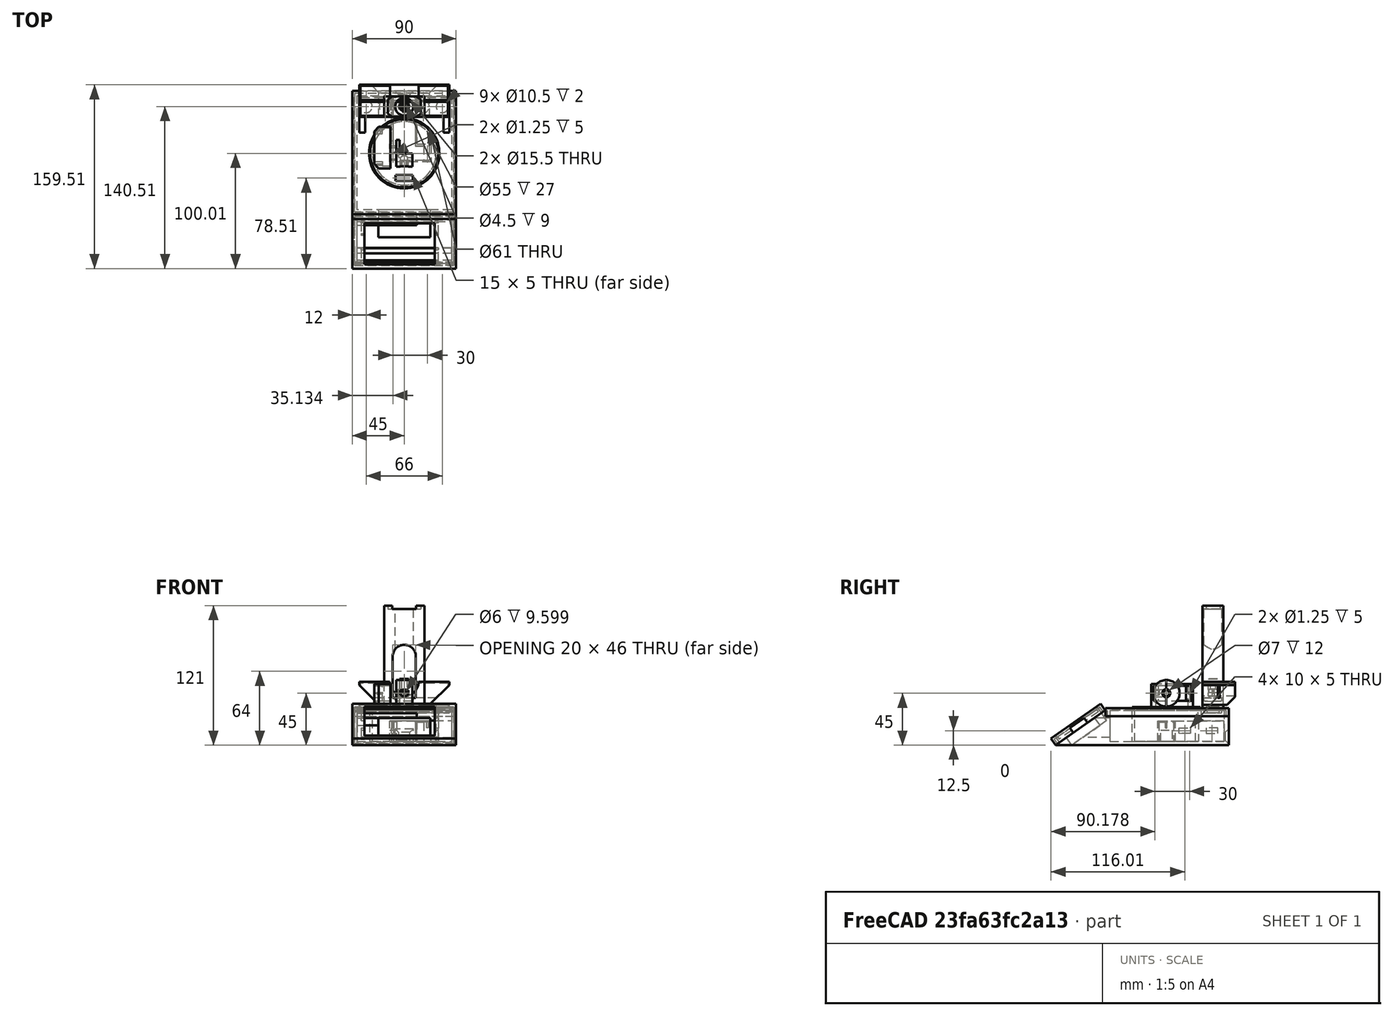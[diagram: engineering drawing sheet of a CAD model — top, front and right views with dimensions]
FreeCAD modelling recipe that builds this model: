
FCSTD DOCUMENT  (FreeCAD 0.18R16131 (Git))
Label: Laser_Projection_Microscope
License: All rights reserved
LicenseURL: http://en.wikipedia.org/wiki/All_rights_reserved
objects: Sketcher::SketchObject×63, PartDesign::Pocket×45, PartDesign::Pad×17, PartDesign::Body×8, Mesh::Feature×6, PartDesign::Chamfer×3, PartDesign::LinearPattern×3, PartDesign::Fillet×1
note: 202 computed .brp shape members not serialized (recipe doc carries the construction recipe); baked Part::Feature solids carry a one-line shape summary decoded from their .brp

FEATURE [Mesh::Feature] Nextion_2_4  label="Nextion 2.4"
  Placement = pos=(0,98.8389,144.254) rot=(0.287968,0.287968,-0.913318;1.66134rad)
FEATURE [Mesh::Feature] Arduino_Nano_wo_Mounts
  Placement = pos=(4.9631e-12,17,4) rot=(0,0,1;3.14159rad)
FEATURE [Sketcher::SketchObject] Sketch004  label="Sketch_Rect-Base-Cut"
  MapMode = 5
  Placement = pos=(45,0,0) rot=(0.57735,0.57735,0.57735;2.0944rad)
  sketch-geometry (3):
    g0: LineSegment StartX=-107 StartY=0 StartZ=0 EndX=-107 EndY=30 EndZ=0
    g1: LineSegment StartX=-107 StartY=30 StartZ=0 EndX=-64 EndY=30 EndZ=0
    g2: LineSegment StartX=-64 StartY=30 StartZ=0 EndX=-107 EndY=0 EndZ=0
  constraints (9):
    c: PointOnObject(g0,g-1)
    c: Vertical(g0)
    c: Coincident(g0,g1)
    c: Horizontal(g1)
    c: Coincident(g1,g2)
    c: Coincident(g2,g0)
    c: DistanceY(g0,g0) = 30
    c: DistanceX(g0,g-1) = 107
    c: DistanceX(g1,g1) = 43
FEATURE [Sketcher::SketchObject] Sketch019  label="Sketch_Cap-Screen-Base"
  MapMode = 5
  Support = -> [XY_Plane001]
  sketch-geometry (4):
    g0: LineSegment StartX=-45 StartY=52.43 StartZ=0 EndX=45 EndY=52.43 EndZ=0
    g1: LineSegment StartX=45 StartY=52.43 StartZ=0 EndX=45 EndY=0 EndZ=0
    g2: LineSegment StartX=45 StartY=0 StartZ=0 EndX=-45 EndY=0 EndZ=0
    g3: LineSegment StartX=-45 StartY=0 StartZ=0 EndX=-45 EndY=52.43 EndZ=0
  constraints (11):
    c: Coincident(g0,g1)
    c: Coincident(g1,g2)
    c: Coincident(g2,g3)
    c: Coincident(g3,g0)
    c: Horizontal(g0)
    c: Horizontal(g2)
    c: Vertical(g1)
    c: Vertical(g3)
    c: Symmetric(g2,g1,g-1)
    c: DistanceX(g2,g2) = 90
    c: DistanceY(g3,g3) = 52.43
FEATURE [PartDesign::Pad] Pad008  label="Pad_Cap-Screen-Base"
  Length = 7
  Length2 = 100
  Profile = -> Sketch019
  Type = 0
FEATURE [Sketcher::SketchObject] Sketch020  label="Sketch_Cap-Screen-Base-Hole"
  MapMode = 5
  Placement = pos=(0,0,0) rot=(1,0,0;3.14159rad)
  Support = -> [Pad008]
  sketch-geometry (4):
    g0: LineSegment StartX=-43 StartY=-2 StartZ=0 EndX=43 EndY=-2 EndZ=0
    g1: LineSegment StartX=43 StartY=-2 StartZ=0 EndX=43 EndY=-50.43 EndZ=0
    g2: LineSegment StartX=43 StartY=-50.43 StartZ=0 EndX=-43 EndY=-50.43 EndZ=0
    g3: LineSegment StartX=-43 StartY=-50.43 StartZ=0 EndX=-43 EndY=-2 EndZ=0
  constraints (11):
    c: Coincident(g0,g1)
    c: Coincident(g1,g2)
    c: Coincident(g2,g3)
    c: Coincident(g3,g0)
    c: Horizontal(g2)
    c: Vertical(g1)
    c: Vertical(g3)
    c: Symmetric(g0,g0,g-2)
    c: DistanceY(g0,g-1) = 2
    c: DistanceY(g3,g3) = 48.43
    c: DistanceX(g0,g0) = 86
FEATURE [PartDesign::Pocket] Pocket010  label="Pocket_Cap-Screen-Base"
  BaseFeature = -> Pad008
  Length = 5
  Length2 = 100
  Profile = -> Sketch020
  Type = 0
FEATURE [Sketcher::SketchObject] Sketch021  label="Sketch_Cap-Screen-Screen"
  MapMode = 5
  Placement = pos=(0,0,7) rot=(0,0,1;0rad)
  Support = -> [Pocket010]
  sketch-geometry (4):
    g0: LineSegment StartX=-34.5 StartY=48 StartZ=0 EndX=26.5 EndY=48 EndZ=0
    g1: LineSegment StartX=26.5 StartY=48 StartZ=0 EndX=26.5 EndY=4.5 EndZ=0
    g2: LineSegment StartX=26.5 StartY=4.5 StartZ=0 EndX=-34.5 EndY=4.5 EndZ=0
    g3: LineSegment StartX=-34.5 StartY=4.5 StartZ=0 EndX=-34.5 EndY=48 EndZ=0
  constraints (11):
    c: Coincident(g0,g1)
    c: Coincident(g1,g2)
    c: Coincident(g2,g3)
    c: Coincident(g3,g0)
    c: Horizontal(g2)
    c: Vertical(g1)
    c: Vertical(g3)
    c: DistanceY(g-1,g2) = 4.5
    c: DistanceY(g3,g3) = 43.5
    c: DistanceX(g2,g2) = 61
    c: DistanceX(g2,g-1) = 34.5
FEATURE [Sketcher::SketchObject] Sketch030  label="Sketch_Cap-Screen-Screen-Spacers"
  MapMode = 5
  Placement = pos=(0,0,5) rot=(1,0,0;3.14159rad)
  Support = -> [Pocket010]
  sketch-geometry (4):
    g0: LineSegment StartX=-37.5 StartY=-5.5 StartZ=0 EndX=29.5 EndY=-5.5 EndZ=0
    g1: LineSegment StartX=29.5 StartY=-5.5 StartZ=0 EndX=29.5 EndY=-47 EndZ=0
    g2: LineSegment StartX=29.5 StartY=-47 StartZ=0 EndX=-37.5 EndY=-47 EndZ=0
    g3: LineSegment StartX=-37.5 StartY=-47 StartZ=0 EndX=-37.5 EndY=-5.5 EndZ=0
  constraints (11):
    c: Coincident(g0,g1)
    c: Coincident(g1,g2)
    c: Coincident(g2,g3)
    c: Coincident(g3,g0)
    c: Horizontal(g2)
    c: Vertical(g1)
    c: Vertical(g3)
    c: DistanceY(g3,g3) = 41.5
    c: DistanceX(g2,g2) = 67
    c: DistanceY(g0,g-1) = 5.5
    c: DistanceX(g2,g-1) = 37.5
FEATURE [PartDesign::Pad] Pad011  label="Pad_Cap-Screen-Screen-Spacers"
  BaseFeature = -> Pocket010
  Length = 2.5
  Length2 = 100
  Profile = -> Sketch030
  Type = 0
FEATURE [PartDesign::Pocket] Pocket011  label="Pocket_Cap-Screen-Screen"
  BaseFeature = -> Pad011
  Length = 5
  Length2 = 100
  Profile = -> Sketch021
  Type = 1
FEATURE [Sketcher::SketchObject] Sketch029  label="Sketch_Cap-Screen_Hole-Cables"
  MapMode = 5
  Placement = pos=(0,0,0) rot=(1,0,0;3.14159rad)
  Support = -> [Pocket011]
  sketch-geometry (4):
    g0: LineSegment StartX=-45 StartY=-18.71 StartZ=0 EndX=45 EndY=-18.71 EndZ=0
    g1: LineSegment StartX=45 StartY=-18.71 StartZ=0 EndX=45 EndY=-33.71 EndZ=0
    g2: LineSegment StartX=45 StartY=-33.71 StartZ=0 EndX=-45 EndY=-33.71 EndZ=0
    g3: LineSegment StartX=-45 StartY=-33.71 StartZ=0 EndX=-45 EndY=-18.71 EndZ=0
  constraints (12):
    c: Coincident(g0,g1)
    c: Coincident(g1,g2)
    c: Coincident(g2,g3)
    c: Coincident(g3,g0)
    c: Horizontal(g0)
    c: Horizontal(g2)
    c: Vertical(g1)
    c: Vertical(g3)
    c: DistanceY(g3,g3) = 15
    c: DistanceY(g0,g-1) = 18.71
    c: DistanceX(g0,g-1) = 45
    c: DistanceX(g2,g2) = 90
FEATURE [PartDesign::Pocket] Pocket016  label="Pocket_Cap-Screen_Hole-Cables"
  BaseFeature = -> Pocket011
  Length = 5
  Length2 = 100
  Profile = -> Sketch029
  Type = 0
FEATURE [PartDesign::Body] Body001  label="Body_Cap-Screen"
  Group = -> [Sketch019,Pad008,Sketch020,Pocket010,Pad011,Sketch030,Sketch021,Pocket011,Sketch029,Pocket016]
  Origin = -> Origin001
  Placement = pos=(0,-107,0) rot=(1,0,0;0.60912rad)
  Tip = -> Pocket016
FEATURE [Sketcher::SketchObject] Sketch033
  MapMode = 5
  Placement = pos=(0,0,2) rot=(0,0,1;0rad)
  sketch-geometry (3):
    g0: LineSegment StartX=-41 StartY=38.816 StartZ=0 EndX=41 EndY=-60.184 EndZ=0
    g1: LineSegment StartX=41 StartY=38.816 StartZ=0 EndX=-41 EndY=-60.184 EndZ=0
    g2: Circle CenterX=0.0132459 CenterY=-10.7 CenterZ=0 NormalX=0 NormalY=0 NormalZ=1 AngleXU=0 Radius=30
  constraints (7):
    c: Symmetric(g0,g1,g-2)
    c: Symmetric(g1,g0,g-2)
    c: DistanceX(g0,g1) = 82
    c: DistanceY(g1,g0) = 99
    c: PointOnObject(g2,g0)
    c: Diameter(g2) = 60
    c: DistanceY(g2,g-1) = 10.7
FEATURE [Mesh::Feature] Servo  label="Servo_Turn-Table"
  Placement = pos=(5.2,-11,3) rot=(0,0,1;0rad)
FEATURE [Sketcher::SketchObject] Sketch043  label="Sketch_Cap-Base"
  MapMode = 5
  Support = -> [XY_Plane002]
  sketch-geometry (4):
    g0: LineSegment StartX=-45 StartY=43.1 StartZ=0 EndX=45 EndY=43.1 EndZ=0
    g1: LineSegment StartX=45 StartY=43.1 StartZ=0 EndX=45 EndY=-63.8 EndZ=0
    g2: LineSegment StartX=45 StartY=-63.8 StartZ=0 EndX=-45 EndY=-63.8 EndZ=0
    g3: LineSegment StartX=-45 StartY=-63.8 StartZ=0 EndX=-45 EndY=43.1 EndZ=0
  constraints (11):
    c: Coincident(g0,g1)
    c: Coincident(g1,g2)
    c: Coincident(g2,g3)
    c: Coincident(g3,g0)
    c: Horizontal(g2)
    c: Vertical(g1)
    c: Vertical(g3)
    c: DistanceX(g0,g0) = 90
    c: DistanceY(g3,g3) = 106.9
    c: DistanceY(g-1,g0) = 43.1
    c: Symmetric(g0,g0,g-2)
FEATURE [PartDesign::Pad] Pad015  label="Pad_Cap-Base"
  Length = 7
  Length2 = 100
  Profile = -> Sketch043
  Type = 0
FEATURE [Sketcher::SketchObject] Sketch044  label="Sketch_Cap-Hole"
  MapMode = 5
  Placement = pos=(0,0,0) rot=(1,0,0;3.14159rad)
  Support = -> [Pad015]
  sketch-geometry (4):
    g0: LineSegment StartX=-43 StartY=61.8 StartZ=0 EndX=43 EndY=61.8 EndZ=0
    g1: LineSegment StartX=43 StartY=61.8 StartZ=0 EndX=43 EndY=-41.1 EndZ=0
    g2: LineSegment StartX=43 StartY=-41.1 StartZ=0 EndX=-43 EndY=-41.1 EndZ=0
    g3: LineSegment StartX=-43 StartY=-41.1 StartZ=0 EndX=-43 EndY=61.8 EndZ=0
  constraints (11):
    c: Coincident(g0,g1)
    c: Coincident(g1,g2)
    c: Coincident(g2,g3)
    c: Coincident(g3,g0)
    c: Horizontal(g0)
    c: Vertical(g1)
    c: Vertical(g3)
    c: Symmetric(g2,g1,g-2)
    c: DistanceX(g2,g2) = 86
    c: DistanceY(g1,g1) = 102.9
    c: DistanceY(g2,g-1) = 41.1
FEATURE [PartDesign::Pocket] Pocket025  label="Pocket_Cap-Hole"
  BaseFeature = -> Pad015
  Length = 5
  Length2 = 100
  Profile = -> Sketch044
  Type = 0
FEATURE [Sketcher::SketchObject] Sketch045  label="Sketch_Cap-Circular-Hole"
  MapMode = 5
  Placement = pos=(0,0,7) rot=(0,0,1;0rad)
  Support = -> [Pocket025]
  sketch-geometry (1):
    g0: Circle CenterX=0 CenterY=-11 CenterZ=0 NormalX=0 NormalY=0 NormalZ=1 AngleXU=0 Radius=30.5
  constraints (3):
    c: PointOnObject(g0,g-2)
    c: Diameter(g0) = 61
    c: DistanceY(g0,g-1) = 11
FEATURE [PartDesign::Pocket] Pocket026  label="Pocket_Cap-Circular-Hole"
  BaseFeature = -> Pocket025
  Length = 5
  Length2 = 100
  Profile = -> Sketch045
  Type = 2
FEATURE [Sketcher::SketchObject] Sketch046  label="Sketch_Turn-Table-Base"
  MapMode = 5
  Support = -> [XY_Plane003]
  sketch-geometry (1):
    g0: Circle CenterX=0 CenterY=-11 CenterZ=0 NormalX=0 NormalY=0 NormalZ=1 AngleXU=0 Radius=29.5
  constraints (3):
    c: PointOnObject(g0,g-2)
    c: DistanceY(g0,g-1) = 11
    c: Diameter(g0) = 59
FEATURE [PartDesign::Pad] Pad016  label="Pad_Turn-Table-Base"
  Length = 3
  Length2 = 100
  Profile = -> Sketch046
  Type = 0
FEATURE [Sketcher::SketchObject] Sketch003  label="Sketch_Rect-Base"
  MapMode = 5
  Placement = pos=(0,0,0) rot=(1,0,0;3.14159rad)
  Support = -> [Pad016]
  sketch-geometry (4):
    g0: LineSegment StartX=-45 StartY=106.9 StartZ=0 EndX=45 EndY=106.9 EndZ=0
    g1: LineSegment StartX=45 StartY=106.9 StartZ=0 EndX=45 EndY=-43.1 EndZ=0
    g2: LineSegment StartX=45 StartY=-43.1 StartZ=0 EndX=-45 EndY=-43.1 EndZ=0
    g3: LineSegment StartX=-45 StartY=-43.1 StartZ=0 EndX=-45 EndY=106.9 EndZ=0
  constraints (11):
    c: Coincident(g0,g1)
    c: Coincident(g1,g2)
    c: Coincident(g2,g3)
    c: Coincident(g3,g0)
    c: Horizontal(g2)
    c: Vertical(g1)
    c: Vertical(g3)
    c: DistanceY(g1,g1) = 150
    c: DistanceX(g0,g0) = 90
    c: Symmetric(g0,g0,g-2)
    c: DistanceY(g-1,g0) = 106.9
FEATURE [PartDesign::Pad] Pad002  label="Pad_Rect-Base"
  Length = 30
  Length2 = 100
  Profile = -> Sketch003
  Reversed = true
  Type = 0
FEATURE [PartDesign::Pocket] Pocket001  label="Pocket_Rect-Base-Cut"
  BaseFeature = -> Pad002
  Length = 5
  Length2 = 100
  Profile = -> Sketch004
  Type = 1
FEATURE [Sketcher::SketchObject] Sketch005  label="Sketch_Rect-Base-Top"
  MapMode = 5
  Placement = pos=(0,-35.0309,50.211) rot=(1,0,0;0.609163rad)
  Support = -> [Pocket001]
  sketch-geometry (4):
    g0: LineSegment StartX=-43 StartY=-37.38 StartZ=0 EndX=43 EndY=-37.38 EndZ=0
    g1: LineSegment StartX=43 StartY=-37.38 StartZ=0 EndX=43 EndY=-85.81 EndZ=0
    g2: LineSegment StartX=43 StartY=-85.81 StartZ=0 EndX=-43 EndY=-85.81 EndZ=0
    g3: LineSegment StartX=-43 StartY=-85.81 StartZ=0 EndX=-43 EndY=-37.38 EndZ=0
  constraints (11):
    c: Coincident(g0,g1)
    c: Coincident(g1,g2)
    c: Coincident(g2,g3)
    c: Coincident(g3,g0)
    c: Horizontal(g0)
    c: Vertical(g1)
    c: Vertical(g3)
    c: Symmetric(g2,g1,g-2)
    c: DistanceY(g3,g3) = 48.43
    c: DistanceX(g0,g0) = 86
    c: DistanceY(g0,g-1) = 37.38
FEATURE [PartDesign::Pad] Pad003  label="Pad_Rect-Base-Cut"
  BaseFeature = -> Pocket001
  Length = 5
  Length2 = 100
  Profile = -> Sketch005
  Type = 0
FEATURE [Sketcher::SketchObject] Sketch006  label="Sketch_Rect-Base-Hole"
  MapMode = 5
  Placement = pos=(0,-37.8918,54.3116) rot=(1,0,0;0.609163rad)
  Support = -> [Pad003]
  sketch-geometry (4):
    g0: LineSegment StartX=-41 StartY=-39.38 StartZ=0 EndX=41 EndY=-39.38 EndZ=0
    g1: LineSegment StartX=41 StartY=-39.38 StartZ=0 EndX=41 EndY=-83.81 EndZ=0
    g2: LineSegment StartX=41 StartY=-83.81 StartZ=0 EndX=-41 EndY=-83.81 EndZ=0
    g3: LineSegment StartX=-41 StartY=-83.81 StartZ=0 EndX=-41 EndY=-39.38 EndZ=0
  constraints (11):
    c: Coincident(g0,g1)
    c: Coincident(g1,g2)
    c: Coincident(g2,g3)
    c: Coincident(g3,g0)
    c: Horizontal(g0)
    c: Vertical(g1)
    c: Vertical(g3)
    c: Symmetric(g2,g1,g-2)
    c: DistanceY(g3,g3) = 44.43
    c: DistanceX(g0,g0) = 82
    c: DistanceY(g0,g-1) = 39.38
FEATURE [PartDesign::Pocket] Pocket002  label="Pocket_Rect-Base-Hole"
  BaseFeature = -> Pad003
  Length = 5
  Length2 = 100
  Profile = -> Sketch006
  Type = 0
FEATURE [Sketcher::SketchObject] Sketch007  label="Sketch_Rect-Base-Cables"
  MapMode = 5
  Placement = pos=(0,-35.0309,50.211) rot=(1,0,0;0.609163rad)
  Support = -> [Pocket002]
  sketch-geometry (4):
    g0: LineSegment StartX=-41 StartY=-46.595 StartZ=0 EndX=41 EndY=-46.595 EndZ=0
    g1: LineSegment StartX=41 StartY=-46.595 StartZ=0 EndX=41 EndY=-76.595 EndZ=0
    g2: LineSegment StartX=41 StartY=-76.595 StartZ=0 EndX=-41 EndY=-76.595 EndZ=0
    g3: LineSegment StartX=-41 StartY=-76.595 StartZ=0 EndX=-41 EndY=-46.595 EndZ=0
  constraints (11):
    c: Coincident(g0,g1)
    c: Coincident(g1,g2)
    c: Coincident(g2,g3)
    c: Coincident(g3,g0)
    c: Horizontal(g2)
    c: Vertical(g1)
    c: Vertical(g3)
    c: DistanceX(g0,g0) = 82
    c: DistanceY(g3,g3) = 30
    c: Symmetric(g0,g0,g-2)
    c: DistanceY(g0,g-1) = 46.595
FEATURE [PartDesign::Pocket] Pocket003  label="Pocket_Rect-Base-Cables"
  BaseFeature = -> Pocket002
  Length = 8
  Length2 = 100
  Profile = -> Sketch007
  Type = 0
FEATURE [Sketcher::SketchObject] Sketch009  label="Sketch_Rect-Base-SD"
  MapMode = 5
  Placement = pos=(0,-35.0309,50.211) rot=(1,0,0;0.609163rad)
  Support = -> [Pocket003]
  sketch-geometry (4):
    g0: LineSegment StartX=11 StartY=-39.38 StartZ=0 EndX=41 EndY=-39.38 EndZ=0
    g1: LineSegment StartX=41 StartY=-39.38 StartZ=0 EndX=41 EndY=-54.38 EndZ=0
    g2: LineSegment StartX=41 StartY=-54.38 StartZ=0 EndX=11 EndY=-54.38 EndZ=0
    g3: LineSegment StartX=11 StartY=-54.38 StartZ=0 EndX=11 EndY=-39.38 EndZ=0
  constraints (12):
    c: Coincident(g0,g1)
    c: Coincident(g1,g2)
    c: Coincident(g2,g3)
    c: Coincident(g3,g0)
    c: Horizontal(g0)
    c: Vertical(g1)
    c: Vertical(g3)
    c: DistanceY(g3,g3) = 15
    c: DistanceX(g0,g0) = 30
    c: DistanceY(g0,g-1) = 39.38
    c: DistanceX(g-1,g0) = 41
    c: Horizontal(g2)
FEATURE [PartDesign::Pocket] Pocket004  label="Pocket_Rect-Base-SD"
  BaseFeature = -> Pocket003
  Length = 8
  Length2 = 100
  Profile = -> Sketch009
  Type = 0
FEATURE [Sketcher::SketchObject] Sketch  label="Sketch_Rect-Base-Connection"
  AttachmentOffset = pos=(0,0,-47) rot=(0,0,1;0rad)
  MapMode = 5
  Placement = pos=(0,-59.9,-1.04e-14) rot=(1,0,0;1.5708rad)
  Support = -> [Pocket004]
  sketch-geometry (4):
    g0: LineSegment StartX=-22.5 StartY=23.5 StartZ=0 EndX=22.5 EndY=23.5 EndZ=0
    g1: LineSegment StartX=22.5 StartY=23.5 StartZ=0 EndX=22.5 EndY=6.5 EndZ=0
    g2: LineSegment StartX=22.5 StartY=6.5 StartZ=0 EndX=-22.5 EndY=6.5 EndZ=0
    g3: LineSegment StartX=-22.5 StartY=6.5 StartZ=0 EndX=-22.5 EndY=23.5 EndZ=0
  constraints (11):
    c: Coincident(g0,g1)
    c: Coincident(g1,g2)
    c: Coincident(g2,g3)
    c: Coincident(g3,g0)
    c: Horizontal(g2)
    c: Vertical(g1)
    c: Vertical(g3)
    c: DistanceY(g-1,g2) = 6.5
    c: DistanceY(g1,g1) = 17
    c: DistanceX(g0,g0) = 45
    c: Symmetric(g0,g0,g-2)
FEATURE [PartDesign::Pocket] Pocket  label="Pocket_Rect-Base-Connection"
  BaseFeature = -> Pocket004
  Length = 5
  Length2 = 100
  Profile = -> Sketch
  Reversed = true
  Type = 1
FEATURE [Sketcher::SketchObject] Sketch034  label="Sketch_Rect-Base-Central-Lowering-Hole"
  MapMode = 5
  Placement = pos=(0,0,30) rot=(0,0,1;0rad)
  Support = -> [Pocket]
  sketch-geometry (4):
    g0: LineSegment StartX=-45 StartY=43.1 StartZ=0 EndX=45 EndY=43.1 EndZ=0
    g1: LineSegment StartX=45 StartY=43.1 StartZ=0 EndX=45 EndY=-63.9 EndZ=0
    g2: LineSegment StartX=45 StartY=-63.9 StartZ=0 EndX=-45 EndY=-63.9 EndZ=0
    g3: LineSegment StartX=-45 StartY=-63.9 StartZ=0 EndX=-45 EndY=43.1 EndZ=0
  constraints (11):
    c: Coincident(g0,g1)
    c: Coincident(g1,g2)
    c: Coincident(g2,g3)
    c: Coincident(g3,g0)
    c: Horizontal(g2)
    c: Vertical(g1)
    c: Vertical(g3)
    c: Symmetric(g0,g0,g-2)
    c: DistanceX(g0,g0) = 90
    c: DistanceY(g-1,g0) = 43.1
    c: DistanceY(g1,g1) = 107
FEATURE [PartDesign::Pocket] Pocket017  label="Pocket_Rect-Base-Central-Lowering-Hole"
  BaseFeature = -> Pocket
  Length = 5
  Length2 = 100
  Profile = -> Sketch034
  Type = 0
FEATURE [Sketcher::SketchObject] Sketch031  label="Sketch_Rect-Base-Central-Top"
  MapMode = 5
  Placement = pos=(0,0,25) rot=(0,0,1;0rad)
  Support = -> [Pocket017]
  sketch-geometry (4):
    g0: LineSegment StartX=-43 StartY=41.1 StartZ=0 EndX=43 EndY=41.1 EndZ=0
    g1: LineSegment StartX=43 StartY=41.1 StartZ=0 EndX=43 EndY=-61.9 EndZ=0
    g2: LineSegment StartX=43 StartY=-61.9 StartZ=0 EndX=-43 EndY=-61.9 EndZ=0
    g3: LineSegment StartX=-43 StartY=-61.9 StartZ=0 EndX=-43 EndY=41.1 EndZ=0
  constraints (11):
    c: Coincident(g0,g1)
    c: Coincident(g1,g2)
    c: Coincident(g2,g3)
    c: Coincident(g3,g0)
    c: Horizontal(g2)
    c: Vertical(g1)
    c: Vertical(g3)
    c: Symmetric(g0,g0,g-2)
    c: DistanceX(g0,g0) = 86
    c: DistanceY(g-1,g0) = 41.1
    c: DistanceY(g1,g1) = 103
FEATURE [PartDesign::Pad] Pad  label="Pad_Rect-Base-Central-Top"
  BaseFeature = -> Pocket017
  Length = 5
  Length2 = 100
  Profile = -> Sketch031
  Type = 0
FEATURE [Sketcher::SketchObject] Sketch032  label="Sketch_Rect-Base-Central-Hole"
  MapMode = 5
  Placement = pos=(0,0,30) rot=(0,0,1;0rad)
  Support = -> [Pad]
  sketch-geometry (4):
    g0: LineSegment StartX=-41 StartY=39.1 StartZ=0 EndX=41 EndY=39.1 EndZ=0
    g1: LineSegment StartX=41 StartY=39.1 StartZ=0 EndX=41 EndY=-59.9 EndZ=0
    g2: LineSegment StartX=41 StartY=-59.9 StartZ=0 EndX=-41 EndY=-59.9 EndZ=0
    g3: LineSegment StartX=-41 StartY=-59.9 StartZ=0 EndX=-41 EndY=39.1 EndZ=0
  constraints (11):
    c: Coincident(g0,g1)
    c: Coincident(g1,g2)
    c: Coincident(g2,g3)
    c: Coincident(g3,g0)
    c: Horizontal(g2)
    c: Vertical(g1)
    c: Vertical(g3)
    c: Symmetric(g0,g0,g-2)
    c: DistanceX(g0,g0) = 82
    c: DistanceY(g-1,g0) = 39.1
    c: DistanceY(g1,g1) = 99
FEATURE [PartDesign::Pocket] Pocket018  label="Pocket_Rect-Base-Central-Hole"
  BaseFeature = -> Pad
  Length = 27
  Length2 = 100
  Profile = -> Sketch032
  Type = 0
FEATURE [Sketcher::SketchObject] Sketch036  label="Sketch_Rect-Base-Pad-Round"
  MapMode = 5
  Placement = pos=(0,0,3) rot=(0,0,1;0rad)
  Support = -> [Pocket018]
  sketch-geometry (1):
    g0: Circle CenterX=0 CenterY=-11 CenterZ=0 NormalX=0 NormalY=0 NormalZ=1 AngleXU=0 Radius=30
  constraints (3):
    c: PointOnObject(g0,g-2)
    c: Diameter(g0) = 60
    c: DistanceY(g0,g-1) = 11
FEATURE [PartDesign::Pad] Pad013  label="Pad_Rect-Base-Pad-Round"
  BaseFeature = -> Pocket018
  Length = 27
  Length2 = 100
  Profile = -> Sketch036
  Type = 0
FEATURE [Sketcher::SketchObject] Sketch037  label="Sketch_Rect-Base-Pad-Round-Hole"
  MapMode = 5
  Placement = pos=(0,0,30) rot=(0,0,1;0rad)
  Support = -> [Pad013]
  sketch-geometry (1):
    g0: Circle CenterX=0 CenterY=-11 CenterZ=0 NormalX=0 NormalY=0 NormalZ=1 AngleXU=0 Radius=27.5
  constraints (3):
    c: PointOnObject(g0,g-2)
    c: DistanceY(g0,g-1) = 11
    c: Diameter(g0) = 55
FEATURE [PartDesign::Pocket] Pocket019  label="Pocket_Rect-Base-Pad-Round-Hole"
  BaseFeature = -> Pad013
  Length = 27
  Length2 = 100
  Profile = -> Sketch037
  Type = 0
FEATURE [Sketcher::SketchObject] Sketch035  label="Sketch_Rect-Base-Pad-Elements"
  MapMode = 5
  Placement = pos=(0,0,3) rot=(0,0,1;0rad)
  Support = -> [Pocket019]
  sketch-geometry (8):
    g0: LineSegment StartX=-11 StartY=39 StartZ=0 EndX=11 EndY=39 EndZ=0
    g1: LineSegment StartX=11 StartY=39 StartZ=0 EndX=11 EndY=-3.04259 EndZ=0
    g2: LineSegment StartX=11 StartY=-3.04259 StartZ=0 EndX=23.2659 EndY=-3.04259 EndZ=0
    g3: LineSegment StartX=23.2659 StartY=-3.04259 StartZ=0 EndX=23.2659 EndY=-18.4793 EndZ=0
    g4: LineSegment StartX=23.2659 StartY=-18.4793 StartZ=0 EndX=-12.7089 EndY=-18.4793 EndZ=0
    g5: LineSegment StartX=-12.7089 StartY=-18.4793 StartZ=0 EndX=-12.7089 EndY=-3.04259 EndZ=0
    g6: LineSegment StartX=-12.7089 StartY=-3.04259 StartZ=0 EndX=-11 EndY=-3.04259 EndZ=0
    g7: LineSegment StartX=-11 StartY=-3.04259 StartZ=0 EndX=-11 EndY=39 EndZ=0
  constraints (18):
    c: Coincident(g0,g1)
    c: Vertical(g1)
    c: Coincident(g1,g2)
    c: Horizontal(g2)
    c: Coincident(g2,g3)
    c: Vertical(g3)
    c: Coincident(g3,g4)
    c: Horizontal(g4)
    c: Coincident(g4,g5)
    c: Vertical(g5)
    c: Coincident(g5,g6)
    c: Coincident(g6,g7)
    c: Coincident(g7,g0)
    c: DistanceY(g-1,g0) = 39
    c: Symmetric(g0,g0,g-2)
    c: DistanceX(g0,g0) = 22
    c: Symmetric(g6,g1,g-2)
    c: Equal(g5,g3)
FEATURE [PartDesign::Pad] Pad014  label="Pad_Rect-Base-Pad-Elements"
  BaseFeature = -> Pocket019
  Length = 18
  Length2 = 100
  Profile = -> Sketch035
  Type = 0
FEATURE [Sketcher::SketchObject] Sketch038  label="Sketch_Rect-Base-Pad-Elements-Hole1"
  MapMode = 5
  Placement = pos=(0,0,21) rot=(0,0,1;0rad)
  Support = -> [Pad014]
  sketch-geometry (8):
    g0: LineSegment StartX=-9.5 StartY=39 StartZ=0 EndX=9.5 EndY=39 EndZ=0
    g1: LineSegment StartX=9.5 StartY=39 StartZ=0 EndX=9.5 EndY=-4.75035 EndZ=0
    g2: LineSegment StartX=9.5 StartY=-4.75035 StartZ=0 EndX=16.9308 EndY=-4.75035 EndZ=0
    g3: LineSegment StartX=16.9308 StartY=-4.75035 StartZ=0 EndX=16.9308 EndY=-17.3252 EndZ=0
    g4: LineSegment StartX=16.9308 StartY=-17.3252 StartZ=0 EndX=-6.62122 EndY=-17.3252 EndZ=0
    g5: LineSegment StartX=-6.62122 StartY=-17.3252 StartZ=0 EndX=-6.62122 EndY=-4.75035 EndZ=0
    g6: LineSegment StartX=-6.62122 StartY=-4.75035 StartZ=0 EndX=-9.5 EndY=-4.75035 EndZ=0
    g7: LineSegment StartX=-9.5 StartY=-4.75035 StartZ=0 EndX=-9.5 EndY=39 EndZ=0
  constraints (18):
    c: Coincident(g0,g1)
    c: Vertical(g1)
    c: Coincident(g1,g2)
    c: Horizontal(g2)
    c: Coincident(g2,g3)
    c: Vertical(g3)
    c: Coincident(g3,g4)
    c: Horizontal(g4)
    c: Coincident(g4,g5)
    c: Vertical(g5)
    c: Coincident(g5,g6)
    c: Coincident(g6,g7)
    c: Coincident(g7,g0)
    c: DistanceY(g-1,g0) = 39
    c: Symmetric(g0,g0,g-2)
    c: DistanceX(g0,g0) = 19
    c: Symmetric(g6,g1,g-2)
    c: Equal(g5,g3)
FEATURE [PartDesign::Pocket] Pocket020  label="Pocket_Rect-Base-Pad-Elements-Hole1"
  BaseFeature = -> Pad014
  Length = 18
  Length2 = 100
  Profile = -> Sketch038
  Type = 0
FEATURE [Sketcher::SketchObject] Sketch039  label="Sketch_Rect-Base-Pad-Elements-Hole2"
  MapMode = 5
  Placement = pos=(0,0,21) rot=(0,0,1;0rad)
  Support = -> [Pocket020]
  sketch-geometry (4):
    g0: LineSegment StartX=-11.2081 StartY=-4.57742 StartZ=0 EndX=21.6941 EndY=-4.57742 EndZ=0
    g1: LineSegment StartX=21.6941 StartY=-4.57742 StartZ=0 EndX=21.6941 EndY=-17.3252 EndZ=0
    g2: LineSegment StartX=21.6941 StartY=-17.3252 StartZ=0 EndX=-11.2081 EndY=-17.3252 EndZ=0
    g3: LineSegment StartX=-11.2081 StartY=-17.3252 StartZ=0 EndX=-11.2081 EndY=-4.57742 EndZ=0
  constraints (8):
    c: Coincident(g0,g1)
    c: Coincident(g1,g2)
    c: Coincident(g2,g3)
    c: Coincident(g3,g0)
    c: Horizontal(g0)
    c: Horizontal(g2)
    c: Vertical(g1)
    c: Vertical(g3)
FEATURE [PartDesign::Pocket] Pocket021  label="Pocket_Rect-Base-Pad-Elements-Hole2"
  BaseFeature = -> Pocket020
  Length = 1
  Length2 = 100
  Profile = -> Sketch039
  Type = 0
FEATURE [Sketcher::SketchObject] Sketch040  label="Sketch_Rect-Base-Cable-Hole-Servo"
  MapMode = 5
  Placement = pos=(-12.7089,0,0) rot=(0.57735,-0.57735,-0.57735;2.0944rad)
  Support = -> [Pocket021]
  sketch-geometry (4):
    g0: LineSegment StartX=6 StartY=13 StartZ=0 EndX=16 EndY=13 EndZ=0
    g1: LineSegment StartX=16 StartY=13 StartZ=0 EndX=16 EndY=3 EndZ=0
    g2: LineSegment StartX=16 StartY=3 StartZ=0 EndX=6 EndY=3 EndZ=0
    g3: LineSegment StartX=6 StartY=3 StartZ=0 EndX=6 EndY=13 EndZ=0
  constraints (12):
    c: Coincident(g0,g1)
    c: Coincident(g1,g2)
    c: Coincident(g2,g3)
    c: Coincident(g3,g0)
    c: Horizontal(g0)
    c: Horizontal(g2)
    c: Vertical(g1)
    c: Vertical(g3)
    c: DistanceY(g-1,g1) = 3
    c: DistanceX(g-1,g2) = 6
    c: DistanceX(g2,g2) = 10
    c: DistanceY(g1,g1) = 10
FEATURE [PartDesign::Pocket] Pocket022  label="Pocket_Rect-Base-Cable-Hole-Servo"
  BaseFeature = -> Pocket021
  Length = 5
  Length2 = 100
  Profile = -> Sketch040
  Type = 2
FEATURE [Sketcher::SketchObject] Sketch041  label="Sketch_Rect-Base-Cable-Hole-String"
  MapMode = 5
  Placement = pos=(-11,0,0) rot=(0.57735,-0.57735,-0.57735;2.0944rad)
  Support = -> [Pocket022]
  sketch-geometry (8):
    g0: LineSegment StartX=-10 StartY=15 StartZ=0 EndX=0 EndY=15 EndZ=0
    g1: LineSegment StartX=0 StartY=15 StartZ=0 EndX=0 EndY=10 EndZ=0
    g2: LineSegment StartX=0 StartY=10 StartZ=0 EndX=-10 EndY=10 EndZ=0
    g3: LineSegment StartX=-10 StartY=10 StartZ=0 EndX=-10 EndY=15 EndZ=0
    g4: LineSegment StartX=-33.5394 StartY=15 StartZ=0 EndX=-23.5394 EndY=15 EndZ=0
    g5: LineSegment StartX=-23.5394 StartY=15 StartZ=0 EndX=-23.5394 EndY=10 EndZ=0
    g6: LineSegment StartX=-23.5394 StartY=10 StartZ=0 EndX=-33.5394 EndY=10 EndZ=0
    g7: LineSegment StartX=-33.5394 StartY=10 StartZ=0 EndX=-33.5394 EndY=15 EndZ=0
  constraints (23):
    c: Coincident(g0,g1)
    c: Coincident(g1,g2)
    c: Coincident(g2,g3)
    c: Coincident(g3,g0)
    c: Horizontal(g0)
    c: Horizontal(g2)
    c: Vertical(g1)
    c: Vertical(g3)
    c: PointOnObject(g1,g-2)
    c: Coincident(g4,g5)
    c: Coincident(g5,g6)
    c: Coincident(g6,g7)
    c: Coincident(g7,g4)
    c: Horizontal(g4)
    c: Horizontal(g6)
    c: Vertical(g5)
    c: Vertical(g7)
    c: Equal(g5,g1)
    c: Equal(g0,g4)
    c: DistanceY(g-1,g1) = 10
    c: DistanceY(g-1,g5) = 10
    c: DistanceX(g4,g4) = 10
    c: DistanceY(g7,g7) = 5
FEATURE [PartDesign::Pocket] Pocket023  label="Pocket_Rect-Base-Cable-Hole-String"
  BaseFeature = -> Pocket022
  Length = 22
  Length2 = 100
  Profile = -> Sketch041
  Type = 0
FEATURE [Sketcher::SketchObject] Sketch042  label="Sketch_Rect-Base-Arduino-Hole"
  MapMode = 5
  Placement = pos=(0,43.1,0) rot=(0,0.707107,0.707107;3.14159rad)
  Support = -> [Pocket023]
  sketch-geometry (4):
    g0: LineSegment StartX=-5 StartY=11 StartZ=0 EndX=5 EndY=11 EndZ=0
    g1: LineSegment StartX=5 StartY=11 StartZ=0 EndX=5 EndY=4 EndZ=0
    g2: LineSegment StartX=5 StartY=4 StartZ=0 EndX=-5 EndY=4 EndZ=0
    g3: LineSegment StartX=-5 StartY=4 StartZ=0 EndX=-5 EndY=11 EndZ=0
  constraints (11):
    c: Coincident(g0,g1)
    c: Coincident(g1,g2)
    c: Coincident(g2,g3)
    c: Coincident(g3,g0)
    c: Horizontal(g2)
    c: Vertical(g1)
    c: Vertical(g3)
    c: Symmetric(g0,g0,g-2)
    c: DistanceX(g0,g0) = 10
    c: DistanceY(g1,g1) = 7
    c: DistanceY(g-1,g1) = 4
FEATURE [PartDesign::Pocket] Pocket024  label="Pocket_Rect-Base-Arduino-Hole"
  BaseFeature = -> Pocket023
  Length = 5
  Length2 = 100
  Profile = -> Sketch042
  Type = 2
FEATURE [PartDesign::Chamfer] Chamfer
  Base = -> Pocket024 [Edge31,Edge30,Edge32,Edge29]
  BaseFeature = -> Pocket024
  Size = 3
FEATURE [Sketcher::SketchObject] Sketch047  label="Sketch_Turn-Table-Hole-Servo"
  MapMode = 5
  Placement = pos=(0,0,0) rot=(1,0,0;3.14159rad)
  Support = -> [Pad016]
  sketch-geometry (1):
    g0: Circle CenterX=0 CenterY=11 CenterZ=0 NormalX=0 NormalY=0 NormalZ=1 AngleXU=0 Radius=2.25
  constraints (3):
    c: PointOnObject(g0,g-2)
    c: DistanceY(g0,g-1) = -11
    c: Diameter(g0) = 4.5
FEATURE [PartDesign::Pocket] Pocket027  label="Pocket_Turn-Table-Hole-Servo"
  BaseFeature = -> Pad016
  Length = 3
  Length2 = 100
  Profile = -> Sketch047
  Type = 0
FEATURE [Sketcher::SketchObject] Sketch048  label="Sketch_Turn-Table-Hole-Cables"
  MapMode = 5
  Placement = pos=(0,0,3) rot=(0,0,1;0rad)
  Support = -> [Pocket027]
  sketch-geometry (4):
    g0: LineSegment StartX=-7.5 StartY=-30 StartZ=0 EndX=7.5 EndY=-30 EndZ=0
    g1: LineSegment StartX=7.5 StartY=-30 StartZ=0 EndX=7.5 EndY=-35 EndZ=0
    g2: LineSegment StartX=7.5 StartY=-35 StartZ=0 EndX=-7.5 EndY=-35 EndZ=0
    g3: LineSegment StartX=-7.5 StartY=-35 StartZ=0 EndX=-7.5 EndY=-30 EndZ=0
  constraints (11):
    c: Coincident(g0,g1)
    c: Coincident(g1,g2)
    c: Coincident(g2,g3)
    c: Coincident(g3,g0)
    c: Horizontal(g2)
    c: Vertical(g1)
    c: Vertical(g3)
    c: Symmetric(g0,g0,g-2)
    c: DistanceX(g2,g2) = 15
    c: DistanceY(g1,g1) = 5
    c: DistanceY(g0,g-1) = 30
FEATURE [PartDesign::Pocket] Pocket028  label="Pocket_Turn-Table-Hole-Cables"
  BaseFeature = -> Pocket027
  Length = 5
  Length2 = 100
  Profile = -> Sketch048
  Type = 0
FEATURE [Sketcher::SketchObject] Sketch049  label="Sketch_Rect-Base-Screws"
  MapMode = 5
  Placement = pos=(0,0,20) rot=(0,0,1;0rad)
  Support = -> [Chamfer]
  sketch-geometry (2):
    g0: Circle CenterX=-9.86578 CenterY=-11 CenterZ=0 NormalX=0 NormalY=0 NormalZ=1 AngleXU=0 Radius=0.625
    g1: Circle CenterX=20.1342 CenterY=-11 CenterZ=0 NormalX=0 NormalY=0 NormalZ=1 AngleXU=0 Radius=0.625
  constraints (5):
    c: DistanceY(g0,g-1) = 11
    c: DistanceY(g1,g-1) = 11
    c: DistanceX(g0,g1) = 30
    c: Diameter(g0) = 1.25
    c: Equal(g0,g1)
FEATURE [PartDesign::Pocket] Pocket029  label="Pocket_Rect-Base-Screws"
  BaseFeature = -> Chamfer
  Length = 5
  Length2 = 100
  Profile = -> Sketch049
  Type = 0
FEATURE [PartDesign::Body] Body  label="Body_Main-Block"
  Group = -> [Pad002,Sketch003,Sketch004,Pocket001,Sketch005,Pad003,Sketch006,Pocket002,Sketch007,Pocket003,Sketch009,Pocket004,Sketch,Pocket,Pocket017,Sketch034,Sketch033,Sketch032,Sketch031,Pad,Pocket018,Sketch035,Sketch036,Pad013,Sketch037,Pocket019,Pad014,Sketch038,Pocket020,Sketch039,Pocket021,Sketch040,Pocket022,Sketch041,Pocket023,Sketch042,Pocket024,Chamfer,Sketch049,Pocket029]
  Origin = -> Origin
  Tip = -> Pocket029
FEATURE [Mesh::Feature] Servo001  label="Servo_Laser"
  Placement = pos=(-34.0429,-5.8,45) rot=(0.57735,0.57735,0.57735;2.0944rad)
FEATURE [Mesh::Feature] Laser
  Placement = pos=(-35,-20.6,45) rot=(1,0,0;4.71239rad)
FEATURE [Sketcher::SketchObject] Sketch050  label="Sketch_Turn-Table-Servo-Base"
  MapMode = 5
  Placement = pos=(0,0,3) rot=(0,0,1;0rad)
  Support = -> [Pocket028]
  sketch-geometry (4):
    g0: LineSegment StartX=-12 StartY=12 StartZ=0 EndX=-26 EndY=12 EndZ=0
    g1: LineSegment StartX=-26 StartY=12 StartZ=0 EndX=-26 EndY=-24 EndZ=0
    g2: LineSegment StartX=-26 StartY=-24 StartZ=0 EndX=-12 EndY=-24 EndZ=0
    g3: LineSegment StartX=-12 StartY=-24 StartZ=0 EndX=-12 EndY=12 EndZ=0
  constraints (12):
    c: Coincident(g0,g1)
    c: Coincident(g1,g2)
    c: Coincident(g2,g3)
    c: Coincident(g3,g0)
    c: Horizontal(g0)
    c: Horizontal(g2)
    c: Vertical(g1)
    c: Vertical(g3)
    c: DistanceY(g-1,g0) = 12
    c: DistanceY(g3,g3) = 36
    c: DistanceX(g0,g0) = 14
    c: DistanceX(g0,g-1) = 12
FEATURE [PartDesign::Pad] Pad017  label="Pad_Turn-Table-Servo-Base"
  BaseFeature = -> Pocket028
  Length = 20
  Length2 = 100
  Profile = -> Sketch050
  Type = 0
FEATURE [Sketcher::SketchObject] Sketch051  label="Sketch_Turn-Table-Servo-Hole1"
  MapMode = 5
  Placement = pos=(-26,0,0) rot=(0.57735,-0.57735,-0.57735;2.0944rad)
  Support = -> [Pad017]
  sketch-geometry (4):
    g0: LineSegment StartX=-6 StartY=21.5 StartZ=0 EndX=18 EndY=21.5 EndZ=0
    g1: LineSegment StartX=18 StartY=21.5 StartZ=0 EndX=18 EndY=8.5 EndZ=0
    g2: LineSegment StartX=18 StartY=8.5 StartZ=0 EndX=-6 EndY=8.5 EndZ=0
    g3: LineSegment StartX=-6 StartY=8.5 StartZ=0 EndX=-6 EndY=21.5 EndZ=0
  constraints (12):
    c: Coincident(g0,g1)
    c: Coincident(g1,g2)
    c: Coincident(g2,g3)
    c: Coincident(g3,g0)
    c: Horizontal(g0)
    c: Horizontal(g2)
    c: Vertical(g1)
    c: Vertical(g3)
    c: DistanceY(g-1,g2) = 8.5
    c: DistanceX(g2,g-1) = 6
    c: DistanceX(g2,g2) = 24
    c: DistanceY(g3,g3) = 13
FEATURE [PartDesign::Pocket] Pocket030  label="Pocket_Turn-Table-Servo-Hole1"
  BaseFeature = -> Pad017
  Length = 5
  Length2 = 100
  Profile = -> Sketch051
  Type = 2
FEATURE [Sketcher::SketchObject] Sketch052  label="Sketch_Turn-Table-Servo-Hole2"
  MapMode = 5
  Placement = pos=(-12,0,0) rot=(0.57735,0.57735,0.57735;2.0944rad)
  Support = -> [Pocket030]
  sketch-geometry (4):
    g0: LineSegment StartX=-22.25 StartY=21.5 StartZ=0 EndX=10.75 EndY=21.5 EndZ=0
    g1: LineSegment StartX=10.75 StartY=21.5 StartZ=0 EndX=10.75 EndY=8.5 EndZ=0
    g2: LineSegment StartX=10.75 StartY=8.5 StartZ=0 EndX=-22.25 EndY=8.5 EndZ=0
    g3: LineSegment StartX=-22.25 StartY=8.5 StartZ=0 EndX=-22.25 EndY=21.5 EndZ=0
  constraints (12):
    c: Coincident(g0,g1)
    c: Coincident(g1,g2)
    c: Coincident(g2,g3)
    c: Coincident(g3,g0)
    c: Horizontal(g0)
    c: Horizontal(g2)
    c: Vertical(g1)
    c: Vertical(g3)
    c: DistanceY(g1,g1) = 13
    c: DistanceY(g-1,g1) = 8.5
    c: DistanceX(g0,g0) = 33
    c: DistanceX(g-1,g1) = 10.75
FEATURE [PartDesign::Pocket] Pocket031  label="Pocket_Turn-Table-Servo-Hole2"
  BaseFeature = -> Pocket030
  Length = 7
  Length2 = 100
  Profile = -> Sketch052
  Type = 0
FEATURE [Sketcher::SketchObject] Sketch053  label="Sketch_Turn-Table-Servo-Screws"
  MapMode = 5
  Placement = pos=(-19,0,0) rot=(0.57735,0.57735,0.57735;2.0944rad)
  Support = -> [Pocket031]
  sketch-geometry (2):
    g0: Circle CenterX=-20.8319 CenterY=15 CenterZ=0 NormalX=0 NormalY=0 NormalZ=1 AngleXU=0 Radius=0.625
    g1: Circle CenterX=9.16808 CenterY=15 CenterZ=0 NormalX=0 NormalY=0 NormalZ=1 AngleXU=0 Radius=0.625
  constraints (5):
    c: DistanceY(g-1,g0) = 15
    c: DistanceY(g-1,g1) = 15
    c: DistanceX(g0,g1) = 30
    c: Diameter(g1) = 1.25
    c: Equal(g1,g0)
FEATURE [PartDesign::Pocket] Pocket032  label="Pocket_Turn-Table-Servo-Screws"
  BaseFeature = -> Pocket031
  Length = 5
  Length2 = 100
  Profile = -> Sketch053
  Type = 0
FEATURE [PartDesign::Chamfer] Chamfer001
  Base = -> Pocket032 [Edge27,Edge29]
  BaseFeature = -> Pocket032
  Size = 4
FEATURE [PartDesign::Body] Body003  label="Body_Turn-Table"
  Group = -> [Sketch046,Pad016,Sketch047,Pocket027,Sketch048,Pocket028,Sketch050,Pad017,Sketch051,Pocket030,Sketch052,Pocket031,Sketch053,Pocket032,Chamfer001]
  Origin = -> Origin003
  Placement = pos=(0,0,30) rot=(0,0,1;0rad)
  Tip = -> Chamfer001
FEATURE [Sketcher::SketchObject] Sketch054  label="Sketch_Laser-Base"
  MapMode = 5
  Placement = pos=(0,0,0) rot=(0.57735,0.57735,0.57735;2.0944rad)
  Support = -> [YZ_Plane004]
  sketch-geometry (1):
    g0: Circle CenterX=-11 CenterY=45 CenterZ=0 NormalX=0 NormalY=0 NormalZ=1 AngleXU=0 Radius=11.5
  constraints (3):
    c: DistanceY(g0) = 45
    c: DistanceX(g0,g-1) = 11
    c: Diameter(g0) = 23
FEATURE [PartDesign::Pad] Pad018  label="Pad_Laser-Base"
  Length = 14
  Length2 = 100
  Placement = pos=(0,0,0) rot=(0.57735,0.57735,0.57735;2.0944rad)
  Profile = -> Sketch054
  Type = 0
FEATURE [Sketcher::SketchObject] Sketch055  label="Sketch_Laser-CutHalf"
  MapMode = 5
  Placement = pos=(14,-3.1e-15,3.1e-15) rot=(0.57735,0.57735,0.57735;2.0944rad)
  Support = -> [Pad018]
  sketch-geometry (4):
    g0: LineSegment StartX=-11 StartY=56.5 StartZ=0 EndX=0.5 EndY=56.5 EndZ=0
    g1: LineSegment StartX=0.5 StartY=56.5 StartZ=0 EndX=0.5 EndY=33.5 EndZ=0
    g2: LineSegment StartX=0.5 StartY=33.5 StartZ=0 EndX=-11 EndY=33.5 EndZ=0
    g3: LineSegment StartX=-11 StartY=33.5 StartZ=0 EndX=-11 EndY=56.5 EndZ=0
  constraints (12):
    c: Coincident(g0,g1)
    c: Coincident(g1,g2)
    c: Coincident(g2,g3)
    c: Coincident(g3,g0)
    c: Horizontal(g0)
    c: Horizontal(g2)
    c: Vertical(g1)
    c: Vertical(g3)
    c: DistanceY(g1,g1) = 23
    c: DistanceY(g-1,g0) = 56.5
    c: DistanceX(g0,g-1) = 11
    c: DistanceX(g0,g0) = 11.5
FEATURE [PartDesign::Pocket] Pocket033  label="Pocket_Laser-CutHalf"
  BaseFeature = -> Pad018
  Length = 11
  Length2 = 100
  Placement = pos=(0,0,0) rot=(0.57735,0.57735,0.57735;2.0944rad)
  Profile = -> Sketch055
  Type = 0
FEATURE [Sketcher::SketchObject] Sketch056  label="Sketch_Laser-Hole"
  MapMode = 5
  Placement = pos=(-9.8e-15,-11,1.2e-15) rot=(0.57735,0.57735,0.57735;4.18879rad)
  Support = -> [Pocket033]
  sketch-geometry (1):
    g0: Circle CenterX=45 CenterY=7 CenterZ=0 NormalX=0 NormalY=0 NormalZ=1 AngleXU=0 Radius=3
  constraints (3):
    c: DistanceY(g-1,g0) = 7
    c: DistanceX(g-1,g0) = 45
    c: Diameter(g0) = 6
FEATURE [PartDesign::Pocket] Pocket034  label="Pocket_Laser-Hole"
  BaseFeature = -> Pocket033
  Length = 5
  Length2 = 100
  Placement = pos=(0,0,0) rot=(0.57735,0.57735,0.57735;2.0944rad)
  Profile = -> Sketch056
  Type = 1
FEATURE [Sketcher::SketchObject] Sketch057  label="Sketch_Laser-Servo-Hole"
  MapMode = 5
  Placement = pos=(-1e-16,0,0) rot=(0.57735,0.57735,-0.57735;4.18879rad)
  Support = -> [Pocket034]
  sketch-geometry (1):
    g0: Circle CenterX=-11 CenterY=-45 CenterZ=0 NormalX=0 NormalY=0 NormalZ=1 AngleXU=0 Radius=2.5
  constraints (3):
    c: DistanceX(g0,g-1) = 11
    c: DistanceY(g0,g-1) = 45
    c: Diameter(g0) = 5
FEATURE [PartDesign::Pocket] Pocket035  label="Pocket_Laser-Servo-Hole"
  BaseFeature = -> Pocket034
  Length = 3
  Length2 = 100
  Placement = pos=(0,0,0) rot=(0.57735,0.57735,0.57735;2.0944rad)
  Profile = -> Sketch057
  Type = 2
FEATURE [Sketcher::SketchObject] Sketch058  label="Sketch_Laser-Screw"
  MapMode = 5
  Placement = pos=(14,-3.1e-15,3.1e-15) rot=(0.57735,0.57735,0.57735;2.0944rad)
  Support = -> [Pocket035]
  sketch-geometry (1):
    g0: Circle CenterX=-11 CenterY=45 CenterZ=0 NormalX=0 NormalY=0 NormalZ=1 AngleXU=0 Radius=3.5
  constraints (3):
    c: DistanceX(g0,g-1) = 11
    c: DistanceY(g-1,g0) = 45
    c: Diameter(g0) = 7
FEATURE [PartDesign::Pocket] Pocket036  label="Pocket_Laser-Screw"
  BaseFeature = -> Pocket035
  Length = 12
  Length2 = 100
  Placement = pos=(0,0,0) rot=(0.57735,0.57735,0.57735;2.0944rad)
  Profile = -> Sketch058
  Type = 0
FEATURE [Sketcher::SketchObject] Sketch059  label="Sketch_Laser-Circuit"
  AttachmentOffset = pos=(0,0,25) rot=(0,0,1;0rad)
  MapMode = 5
  Placement = pos=(0,-25,-5.6e-15) rot=(1,0,0;1.5708rad)
  Support = -> [XZ_Plane004]
  sketch-geometry (4):
    g0: LineSegment StartX=3.5 StartY=47.5 StartZ=0 EndX=10.5 EndY=47.5 EndZ=0
    g1: LineSegment StartX=10.5 StartY=47.5 StartZ=0 EndX=10.5 EndY=43.5 EndZ=0
    g2: LineSegment StartX=10.5 StartY=43.5 StartZ=0 EndX=3.5 EndY=43.5 EndZ=0
    g3: LineSegment StartX=3.5 StartY=43.5 StartZ=0 EndX=3.5 EndY=47.5 EndZ=0
  constraints (12):
    c: Coincident(g0,g1)
    c: Coincident(g1,g2)
    c: Coincident(g2,g3)
    c: Coincident(g3,g0)
    c: Horizontal(g0)
    c: Horizontal(g2)
    c: Vertical(g1)
    c: Vertical(g3)
    c: DistanceX(g0,g0) = 7
    c: DistanceY(g1,g1) = 4
    c: DistanceX(g-1,g0) = 3.5
    c: DistanceY(g-1,g2) = 43.5
FEATURE [PartDesign::Pocket] Pocket037  label="Pocket_Laser-Circuit"
  BaseFeature = -> Pocket036
  Length = 8
  Length2 = 100
  Placement = pos=(0,0,0) rot=(0.57735,0.57735,0.57735;2.0944rad)
  Profile = -> Sketch059
  Type = 0
FEATURE [PartDesign::Body] Body004  label="Body_Laser"
  Group = -> [Sketch054,Pad018,Sketch055,Pocket033,Sketch056,Pocket034,Sketch057,Pocket035,Sketch058,Pocket036,Sketch059,Pocket037]
  Origin = -> Origin004
  Placement = pos=(-7,0,0) rot=(0,0,1;0rad)
  Tip = -> Pocket037
FEATURE [Sketcher::SketchObject] Sketch060  label="Sketch_Cap-Pad-Magnet"
  MapMode = 5
  Placement = pos=(0,0,5) rot=(1,0,0;3.14159rad)
  Support = -> [Pocket026]
  sketch-geometry (4):
    g0: LineSegment StartX=-39 StartY=-22 StartZ=0 EndX=39 EndY=-22 EndZ=0
    g1: LineSegment StartX=39 StartY=-22 StartZ=0 EndX=39 EndY=-37 EndZ=0
    g2: LineSegment StartX=39 StartY=-37 StartZ=0 EndX=-39 EndY=-37 EndZ=0
    g3: LineSegment StartX=-39 StartY=-37 StartZ=0 EndX=-39 EndY=-22 EndZ=0
  constraints (11):
    c: Coincident(g0,g1)
    c: Coincident(g1,g2)
    c: Coincident(g2,g3)
    c: Coincident(g3,g0)
    c: Horizontal(g2)
    c: Vertical(g1)
    c: Vertical(g3)
    c: Symmetric(g0,g0,g-2)
    c: DistanceX(g0,g0) = 78
    c: DistanceY(g1,g1) = 15
    c: DistanceY(g2,g-1) = 37
FEATURE [PartDesign::Pad] Pad019  label="Pad_Cap-Pad-Magnet"
  BaseFeature = -> Pocket026
  Length = 2
  Length2 = 100
  Profile = -> Sketch060
  Type = 0
FEATURE [Sketcher::SketchObject] Sketch061  label="Sketch_Cap-Pocket-Magnet"
  MapMode = 5
  Placement = pos=(0,0,3) rot=(1,0,0;3.14159rad)
  Support = -> [Pad019]
  sketch-geometry (1):
    g0: Circle CenterX=-33 CenterY=-29.5 CenterZ=0 NormalX=0 NormalY=0 NormalZ=1 AngleXU=0 Radius=5.25
  constraints (3):
    c: Diameter(g0) = 10.5
    c: DistanceY(g0,g-1) = 29.5
    c: DistanceX(g0,g-1) = 33
FEATURE [PartDesign::Pocket] Pocket038  label="Pocket_Cap-Pocket-Magnet"
  BaseFeature = -> Pad019
  Length = 2
  Length2 = 100
  Profile = -> Sketch061
  Type = 0
FEATURE [PartDesign::LinearPattern] LinearPattern  label="LinearPattern_Cap-Pocket-Magnet"
  BaseFeature = -> Pocket038
  Direction = -> X_Axis002
  Length = 66
  Occurrences = 5
  Originals = -> [Pocket038]
FEATURE [Sketcher::SketchObject] Sketch062  label="Sketch_Cap-Hole-Cables"
  MapMode = 5
  Placement = pos=(0,0,7) rot=(0,0,1;0rad)
  Support = -> [LinearPattern]
  sketch-geometry (8):
    g0: LineSegment StartX=-39 StartY=22 StartZ=0 EndX=-34 EndY=22 EndZ=0
    g1: LineSegment StartX=-34 StartY=22 StartZ=0 EndX=-34 EndY=7 EndZ=0
    g2: LineSegment StartX=-34 StartY=7 StartZ=0 EndX=-39 EndY=7 EndZ=0
    g3: LineSegment StartX=-39 StartY=7 StartZ=0 EndX=-39 EndY=22 EndZ=0
    g4: LineSegment StartX=34 StartY=22 StartZ=0 EndX=39 EndY=22 EndZ=0
    g5: LineSegment StartX=39 StartY=22 StartZ=0 EndX=39 EndY=7 EndZ=0
    g6: LineSegment StartX=39 StartY=7 StartZ=0 EndX=34 EndY=7 EndZ=0
    g7: LineSegment StartX=34 StartY=7 StartZ=0 EndX=34 EndY=22 EndZ=0
  constraints (22):
    c: Coincident(g0,g1)
    c: Coincident(g1,g2)
    c: Coincident(g2,g3)
    c: Coincident(g3,g0)
    c: Horizontal(g0)
    c: Horizontal(g2)
    c: Vertical(g1)
    c: Vertical(g3)
    c: DistanceX(g0,g0) = 5
    c: DistanceY(g3,g3) = 15
    c: DistanceX(g0,g-1) = 39
    c: DistanceY(g-1,g0) = 22
    c: Coincident(g4,g5)
    c: Coincident(g5,g6)
    c: Coincident(g6,g7)
    c: Coincident(g7,g4)
    c: Horizontal(g4)
    c: Horizontal(g6)
    c: Vertical(g5)
    c: Vertical(g7)
    c: Symmetric(g0,g4,g-2)
    c: Symmetric(g6,g1,g-2)
FEATURE [PartDesign::Pocket] Pocket039  label="Pocket_Cap-Hole-Cables"
  BaseFeature = -> LinearPattern
  Length = 5
  Length2 = 100
  Profile = -> Sketch062
  Type = 1
FEATURE [PartDesign::Body] Body002  label="Body_Cap"
  Group = -> [Sketch043,Pad015,Sketch044,Pocket025,Sketch045,Pocket026,Sketch060,Pad019,Sketch061,Pocket038,LinearPattern,Sketch062,Pocket039]
  Origin = -> Origin002
  Placement = pos=(0,0,25) rot=(0,0,1;0rad)
  Tip = -> Pocket039
FEATURE [Sketcher::SketchObject] Sketch063  label="Sketch_Seringe-Pad-Magnet"
  MapMode = 5
  Support = -> [XY_Plane005]
  sketch-geometry (4):
    g0: LineSegment StartX=-39 StartY=38.5 StartZ=0 EndX=39 EndY=38.5 EndZ=0
    g1: LineSegment StartX=39 StartY=38.5 StartZ=0 EndX=39 EndY=20.5 EndZ=0
    g2: LineSegment StartX=39 StartY=20.5 StartZ=0 EndX=-39 EndY=20.5 EndZ=0
    g3: LineSegment StartX=-39 StartY=20.5 StartZ=0 EndX=-39 EndY=38.5 EndZ=0
  constraints (11):
    c: Coincident(g0,g1)
    c: Coincident(g1,g2)
    c: Coincident(g2,g3)
    c: Coincident(g3,g0)
    c: Horizontal(g2)
    c: Vertical(g1)
    c: Vertical(g3)
    c: DistanceX(g0,g0) = 78
    c: DistanceY(g1,g1) = 18
    c: DistanceY(g-1,g0) = 38.5
    c: Symmetric(g0,g0,g-2)
FEATURE [PartDesign::Pad] Pad020  label="Pad_Seringe-Pad-Magnet"
  Length = 3
  Length2 = 100
  Profile = -> Sketch063
  Type = 0
FEATURE [Sketcher::SketchObject] Sketch064  label="Sketch_Seringe-Pad-Magnet-Hole"
  MapMode = 5
  Placement = pos=(0,0,3) rot=(0,0,1;0rad)
  Support = -> [Pad020]
  sketch-geometry (1):
    g0: Circle CenterX=-33 CenterY=29.5 CenterZ=0 NormalX=0 NormalY=0 NormalZ=1 AngleXU=0 Radius=5.25
  constraints (3):
    c: DistanceX(g0,g-1) = 33
    c: DistanceY(g-1,g0) = 29.5
    c: Diameter(g0) = 10.5
FEATURE [PartDesign::Pocket] Pocket040  label="Pocket_Seringe-Pad-Magnet-Hole"
  BaseFeature = -> Pad020
  Length = 2
  Length2 = 100
  Profile = -> Sketch064
  Type = 0
FEATURE [PartDesign::LinearPattern] LinearPattern001  label="LinearPattern_Seringe-Pad-Magnet-Hole"
  BaseFeature = -> Pocket040
  Direction = -> X_Axis005
  Length = 66
  Occurrences = 2
  Originals = -> [Pocket040]
FEATURE [Mesh::Feature] Seringe
  Placement = pos=(-140,29.5,57.5) rot=(0,0,1;0rad)
FEATURE [Sketcher::SketchObject] Sketch065  label="Sketch_Seringe-Pad"
  MapMode = 5
  Placement = pos=(0,0,3) rot=(0,0,1;0rad)
  Support = -> [LinearPattern001]
  sketch-geometry (4):
    g0: LineSegment StartX=-17.5 StartY=38.5 StartZ=0 EndX=17.5 EndY=38.5 EndZ=0
    g1: LineSegment StartX=17.5 StartY=38.5 StartZ=0 EndX=17.5 EndY=20.5 EndZ=0
    g2: LineSegment StartX=17.5 StartY=20.5 StartZ=0 EndX=-17.5 EndY=20.5 EndZ=0
    g3: LineSegment StartX=-17.5 StartY=20.5 StartZ=0 EndX=-17.5 EndY=38.5 EndZ=0
  constraints (11):
    c: Coincident(g0,g1)
    c: Coincident(g1,g2)
    c: Coincident(g2,g3)
    c: Coincident(g3,g0)
    c: Horizontal(g2)
    c: Vertical(g1)
    c: Vertical(g3)
    c: DistanceY(g1,g1) = 18
    c: DistanceY(g-1,g0) = 38.5
    c: Symmetric(g0,g0,g-2)
    c: DistanceX(g0,g0) = 35
FEATURE [PartDesign::Pad] Pad021  label="Pad_Seringe-Pad"
  BaseFeature = -> LinearPattern001
  Length = 86
  Length2 = 100
  Profile = -> Sketch065
  Type = 0
FEATURE [Sketcher::SketchObject] Sketch066  label="Sketch_Seringe-Pad-Hole"
  MapMode = 5
  Placement = pos=(0,0,89) rot=(0,0,1;0rad)
  Support = -> [Pad021]
  sketch-geometry (1):
    g0: Circle CenterX=0 CenterY=29.5 CenterZ=0 NormalX=0 NormalY=0 NormalZ=1 AngleXU=0 Radius=7.75
  constraints (3):
    c: PointOnObject(g0,g-2)
    c: DistanceY(g-1,g0) = 29.5
    c: Diameter(g0) = 15.5
FEATURE [PartDesign::Pocket] Pocket041  label="Pocket_Seringe-Pad"
  BaseFeature = -> Pad021
  Length = 83
  Length2 = 100
  Profile = -> Sketch066
  Type = 0
FEATURE [Sketcher::SketchObject] Sketch067  label="Sketch_Seringe-Pad-Wings"
  MapMode = 5
  Placement = pos=(0,0,89) rot=(0,0,1;0rad)
  Support = -> [Pocket041]
  sketch-geometry (8):
    g0: LineSegment StartX=-10.25 StartY=38.5 StartZ=0 EndX=10.25 EndY=38.5 EndZ=0
    g1: LineSegment StartX=10.25 StartY=38.5 StartZ=0 EndX=14.25 EndY=35.5 EndZ=0
    g2: LineSegment StartX=14.25 StartY=35.5 StartZ=0 EndX=14.25 EndY=23.5 EndZ=0
    g3: LineSegment StartX=14.25 StartY=23.5 StartZ=0 EndX=10.25 EndY=20.5 EndZ=0
    g4: LineSegment StartX=10.25 StartY=20.5 StartZ=0 EndX=-10.25 EndY=20.5 EndZ=0
    g5: LineSegment StartX=-10.25 StartY=20.5 StartZ=0 EndX=-14.25 EndY=23.5 EndZ=0
    g6: LineSegment StartX=-14.25 StartY=23.5 StartZ=0 EndX=-14.25 EndY=35.5 EndZ=0
    g7: LineSegment StartX=-14.25 StartY=35.5 StartZ=0 EndX=-10.25 EndY=38.5 EndZ=0
  constraints (20):
    c: Coincident(g0,g1)
    c: Coincident(g1,g2)
    c: Vertical(g2)
    c: Coincident(g2,g3)
    c: Coincident(g3,g4)
    c: Coincident(g4,g5)
    c: Coincident(g5,g6)
    c: Coincident(g6,g7)
    c: Coincident(g7,g0)
    c: Symmetric(g0,g0,g-2)
    c: Symmetric(g6,g1,g-2)
    c: Symmetric(g5,g2,g-2)
    c: Symmetric(g4,g3,g-2)
    c: DistanceY(g-1,g0) = 38.5
    c: DistanceX(g6,g1) = 28.5
    c: DistanceY(g3,g0) = 18
    c: DistanceY(g1,g0) = 3
    c: DistanceY(g3,g2) = 3
    c: DistanceX(g0,g1) = 4
    c: DistanceX(g3,g2) = 4
FEATURE [PartDesign::Pocket] Pocket042  label="Pocket_Seringe-Pad-Wings"
  BaseFeature = -> Pocket041
  Length = 3
  Length2 = 100
  Profile = -> Sketch067
  Type = 0
FEATURE [Sketcher::SketchObject] Sketch068  label="Sketch_Seringe-Window"
  MapMode = 5
  Placement = pos=(0,38.5,0) rot=(0,0.707107,0.707107;3.14159rad)
  Support = -> [Pocket042]
  sketch-geometry (4):
    g0: LineSegment StartX=-10 StartY=45 StartZ=0 EndX=10 EndY=45 EndZ=0
    g1: LineSegment StartX=10 StartY=45 StartZ=0 EndX=10 EndY=9 EndZ=0
    g2: LineSegment StartX=10 StartY=9 StartZ=0 EndX=-10 EndY=9 EndZ=0
    g3: LineSegment StartX=-10 StartY=9 StartZ=0 EndX=-10 EndY=45 EndZ=0
  constraints (11):
    c: Coincident(g0,g1)
    c: Coincident(g1,g2)
    c: Coincident(g2,g3)
    c: Coincident(g3,g0)
    c: Horizontal(g2)
    c: Vertical(g1)
    c: Vertical(g3)
    c: Symmetric(g0,g0,g-2)
    c: DistanceY(g-1,g1) = 9
    c: DistanceX(g0,g0) = 20
    c: DistanceY(g1,g1) = 36
FEATURE [PartDesign::Pocket] Pocket043  label="Pocket_Seringe-Window"
  BaseFeature = -> Pocket042
  Length = 5
  Length2 = 100
  Profile = -> Sketch068
  Type = 1
FEATURE [Sketcher::SketchObject] Sketch069  label="Sketch_Seringe-Window-Round"
  MapMode = 5
  Placement = pos=(0,20.5,0) rot=(1,0,0;1.5708rad)
  Support = -> [Pocket043]
  sketch-geometry (1):
    g0: Circle CenterX=0 CenterY=45 CenterZ=0 NormalX=0 NormalY=0 NormalZ=1 AngleXU=0 Radius=10
  constraints (3):
    c: PointOnObject(g0,g-2)
    c: DistanceY(g-1,g0) = 45
    c: Diameter(g0) = 20
FEATURE [PartDesign::Pocket] Pocket044  label="Pocket_Seringe-Window-Round"
  BaseFeature = -> Pocket043
  Length = 5
  Length2 = 100
  Profile = -> Sketch069
  Type = 1
FEATURE [PartDesign::Fillet] Fillet
  Base = -> Pocket044 [Face29]
  BaseFeature = -> Pocket044
  Radius = 1
FEATURE [PartDesign::Body] Body005  label="Body-Seringe"
  Group = -> [Sketch063,Pad020,Sketch064,Pocket040,LinearPattern001,Sketch065,Pad021,Sketch066,Pocket041,Sketch067,Pocket042,Sketch068,Pocket043,Sketch069,Pocket044,Fillet]
  Origin = -> Origin005
  Placement = pos=(0,0,32) rot=(0,0,1;0rad)
  Tip = -> Fillet
FEATURE [Sketcher::SketchObject] Sketch071  label="Sketch_Slide-Pad-Magnet"
  MapMode = 5
  Support = -> [XY_Plane006]
  sketch-geometry (4):
    g0: LineSegment StartX=-39 StartY=38.5 StartZ=0 EndX=39 EndY=38.5 EndZ=0
    g1: LineSegment StartX=39 StartY=38.5 StartZ=0 EndX=39 EndY=20.5 EndZ=0
    g2: LineSegment StartX=39 StartY=20.5 StartZ=0 EndX=-39 EndY=20.5 EndZ=0
    g3: LineSegment StartX=-39 StartY=20.5 StartZ=0 EndX=-39 EndY=38.5 EndZ=0
  constraints (11):
    c: Coincident(g0,g1)
    c: Coincident(g1,g2)
    c: Coincident(g2,g3)
    c: Coincident(g3,g0)
    c: Horizontal(g2)
    c: Vertical(g1)
    c: Vertical(g3)
    c: DistanceX(g0,g0) = 78
    c: DistanceY(g1,g1) = 18
    c: DistanceY(g-1,g0) = 38.5
    c: Symmetric(g0,g0,g-2)
FEATURE [PartDesign::Pad] Pad022  label="Pad_Slide-Pad-Magnet"
  Length = 3
  Length2 = 100
  Profile = -> Sketch071
  Type = 0
FEATURE [Sketcher::SketchObject] Sketch072  label="Sketch_Slide-Pad-Magnet-Hole"
  MapMode = 5
  Placement = pos=(0,0,3) rot=(0,0,1;0rad)
  Support = -> [Pad022]
  sketch-geometry (1):
    g0: Circle CenterX=-33 CenterY=29.5 CenterZ=0 NormalX=0 NormalY=0 NormalZ=1 AngleXU=0 Radius=5.25
  constraints (3):
    c: DistanceX(g0,g-1) = 33
    c: DistanceY(g-1,g0) = 29.5
    c: Diameter(g0) = 10.5
FEATURE [PartDesign::Pocket] Pocket046  label="Pocket_Slide-Pad-Magnet-Hole"
  BaseFeature = -> Pad022
  Length = 2
  Length2 = 100
  Profile = -> Sketch072
  Type = 0
FEATURE [PartDesign::LinearPattern] LinearPattern002  label="LinearPattern_Slide-Pad-Magnet-Hole"
  BaseFeature = -> Pocket046
  Direction = -> X_Axis006
  Length = 66
  Occurrences = 2
  Originals = -> [Pocket046]
FEATURE [Sketcher::SketchObject] Sketch073  label="Sketch_Slide-Pad"
  MapMode = 5
  Placement = pos=(0,0,3) rot=(0,0,1;0rad)
  Support = -> [LinearPattern002]
  sketch-geometry (4):
    g0: LineSegment StartX=-39 StartY=48.5 StartZ=0 EndX=39 EndY=48.5 EndZ=0
    g1: LineSegment StartX=39 StartY=48.5 StartZ=0 EndX=39 EndY=20.5 EndZ=0
    g2: LineSegment StartX=39 StartY=20.5 StartZ=0 EndX=-39 EndY=20.5 EndZ=0
    g3: LineSegment StartX=-39 StartY=20.5 StartZ=0 EndX=-39 EndY=48.5 EndZ=0
  constraints (10):
    c: Coincident(g0,g1)
    c: Coincident(g1,g2)
    c: Coincident(g3,g0)
    c: Horizontal(g2)
    c: Vertical(g1)
    c: Vertical(g3)
    c: DistanceY(g1,g1) = 28
    c: Symmetric(g0,g0,g-2)
    c: DistanceX(g0,g0) = 78
    c: DistanceY(g-1,g2) = 20.5
FEATURE [PartDesign::Pad] Pad023  label="Pad_Slide-Pad"
  BaseFeature = -> LinearPattern002
  Length = 20
  Length2 = 100
  Profile = -> Sketch073
  Type = 0
FEATURE [Sketcher::SketchObject] Sketch078  label="Sketch_Slide-Pad-Hole"
  MapMode = 5
  Placement = pos=(0,20.5,0) rot=(1,0,0;1.5708rad)
  Support = -> [Pad023]
  sketch-geometry (6):
    g0: LineSegment StartX=-39 StartY=3 StartZ=0 EndX=-22 EndY=3 EndZ=0
    g1: LineSegment StartX=-22 StartY=3 StartZ=0 EndX=-39 EndY=20 EndZ=0
    g2: LineSegment StartX=-39 StartY=20 StartZ=0 EndX=-39 EndY=3 EndZ=0
    g3: LineSegment StartX=39 StartY=20 StartZ=0 EndX=39 EndY=3 EndZ=0
    g4: LineSegment StartX=39 StartY=3 StartZ=0 EndX=22 EndY=3 EndZ=0
    g5: LineSegment StartX=22 StartY=3 StartZ=0 EndX=39 EndY=20 EndZ=0
  constraints (15):
    c: Horizontal(g0)
    c: Coincident(g1,g0)
    c: Coincident(g2,g1)
    c: Coincident(g2,g0)
    c: Vertical(g2)
    c: Coincident(g4,g3)
    c: Coincident(g5,g4)
    c: Coincident(g5,g3)
    c: Symmetric(g1,g3,g-2)
    c: Symmetric(g0,g4,g-2)
    c: Symmetric(g0,g3,g-2)
    c: Equal(g2,g0)
    c: DistanceY(g-1,g0) = 3
    c: DistanceX(g0,g3) = 78
    c: DistanceY(g3,g3) = 17
FEATURE [PartDesign::Pocket] Pocket050  label="Pocket_Slide-Pad-Hole"
  BaseFeature = -> Pad023
  Length = 5
  Length2 = 100
  Profile = -> Sketch078
  Type = 1
FEATURE [Sketcher::SketchObject] Sketch075  label="Sketch_Slide-Hole"
  MapMode = 5
  Placement = pos=(0,0,23) rot=(0,0,1;0rad)
  Support = -> [Pocket050]
  sketch-geometry (4):
    g0: LineSegment StartX=-38.0493 StartY=47.5 StartZ=0 EndX=37.9507 EndY=47.5 EndZ=0
    g1: LineSegment StartX=37.9507 StartY=47.5 StartZ=0 EndX=37.9507 EndY=21.5 EndZ=0
    g2: LineSegment StartX=37.9507 StartY=21.5 StartZ=0 EndX=-38.0493 EndY=21.5 EndZ=0
    g3: LineSegment StartX=-38.0493 StartY=21.5 StartZ=0 EndX=-38.0493 EndY=47.5 EndZ=0
  constraints (11):
    c: Coincident(g0,g1)
    c: Coincident(g1,g2)
    c: Coincident(g2,g3)
    c: Coincident(g3,g0)
    c: Horizontal(g0)
    c: Horizontal(g2)
    c: Vertical(g1)
    c: Vertical(g3)
    c: DistanceX(g0,g0) = 76
    c: DistanceY(g1,g1) = 26
    c: DistanceY(g-1,g2) = 21.5
FEATURE [PartDesign::Pocket] Pocket047  label="Pocket_Slide-Hole"
  BaseFeature = -> Pocket050
  Length = 1.5
  Length2 = 100
  Profile = -> Sketch075
  Type = 0
FEATURE [Sketcher::SketchObject] Sketch076  label="Sketch_Slide-Side-Hole"
  MapMode = 5
  Placement = pos=(0,20.5,0) rot=(1,0,0;1.5708rad)
  Support = -> [Pocket047]
  sketch-geometry (1):
    g0: Circle CenterX=0 CenterY=23 CenterZ=0 NormalX=0 NormalY=0 NormalZ=1 AngleXU=0 Radius=12.5
  constraints (3):
    c: PointOnObject(g0,g-2)
    c: DistanceY(g-1,g0) = 23
    c: Diameter(g0) = 25
FEATURE [PartDesign::Pocket] Pocket048  label="Pocket_Slide-Side-Hole"
  BaseFeature = -> Pocket047
  Length = 5
  Length2 = 100
  Profile = -> Sketch076
  Type = 1
FEATURE [Sketcher::SketchObject] Sketch077  label="Sketch_Slide-Top-Hole"
  MapMode = 5
  Placement = pos=(0,0,21.5) rot=(0,0,1;0rad)
  Support = -> [Pocket048]
  sketch-geometry (4):
    g0: LineSegment StartX=-38 StartY=35.25 StartZ=0 EndX=38 EndY=35.25 EndZ=0
    g1: LineSegment StartX=38 StartY=35.25 StartZ=0 EndX=38 EndY=33.75 EndZ=0
    g2: LineSegment StartX=38 StartY=33.75 StartZ=0 EndX=-38 EndY=33.75 EndZ=0
    g3: LineSegment StartX=-38 StartY=33.75 StartZ=0 EndX=-38 EndY=35.25 EndZ=0
  constraints (11):
    c: Coincident(g0,g1)
    c: Coincident(g1,g2)
    c: Coincident(g2,g3)
    c: Coincident(g3,g0)
    c: Horizontal(g2)
    c: Vertical(g1)
    c: Vertical(g3)
    c: Symmetric(g0,g0,g-2)
    c: DistanceX(g0,g0) = 76
    c: DistanceY(g1,g1) = 1.5
    c: DistanceY(g-1,g2) = 33.75
FEATURE [PartDesign::Pocket] Pocket049  label="Pocket_Slide-Top-Hole"
  BaseFeature = -> Pocket048
  Length = 12.5
  Length2 = 100
  Profile = -> Sketch077
  Type = 0
FEATURE [PartDesign::Chamfer] Chamfer002
  Base = -> Pocket049 [Edge18]
  BaseFeature = -> Pocket049
  Size = 7
FEATURE [PartDesign::Body] Body006  label="Body-Slide"
  Group = -> [Sketch071,Pad022,Sketch072,Pocket046,LinearPattern002,Sketch073,Pad023,Pocket050,Sketch075,Pocket047,Sketch076,Pocket048,Sketch077,Pocket049,Sketch078,Chamfer002]
  Origin = -> Origin006
  Placement = pos=(0,0,32) rot=(0,0,1;0rad)
  Tip = -> Chamfer002
FEATURE [Sketcher::SketchObject] Sketch079  label="Sketch_EM-Grid_Base"
  MapMode = 5
  Support = -> [XY_Plane008]
  sketch-geometry (1):
    g0: Circle CenterX=0 CenterY=0 CenterZ=0 NormalX=0 NormalY=0 NormalZ=1 AngleXU=0 Radius=4
  constraints (2):
    c: Coincident(g0,g-1)
    c: Radius(g0) = 4
FEATURE [PartDesign::Pad] Pad024  label="Pad_EM-Grid_Base"
  Length = 15
  Length2 = 100
  Profile = -> Sketch079
  Reversed = true
  Type = 0
FEATURE [Sketcher::SketchObject] Sketch080  label="Sketch_EM-Grid_Central-Hole"
  MapMode = 5
  Support = -> [Pad024]
  sketch-geometry (1):
    g0: Circle CenterX=0 CenterY=0 CenterZ=0 NormalX=0 NormalY=0 NormalZ=1 AngleXU=0 Radius=2.25
  constraints (2):
    c: Coincident(g0,g-1)
    c: Radius(g0) = 2.25
FEATURE [PartDesign::Pocket] Pocket051  label="Pocket_EM-Grid_Central-Hole"
  BaseFeature = -> Pad024
  Length = 9
  Length2 = 100
  Profile = -> Sketch080
  Type = 0
FEATURE [Sketcher::SketchObject] Sketch081  label="Sketch_EM-Grid_Grid-Slit"
  MapMode = 5
  Placement = pos=(0,0,-9) rot=(0,0,1;0rad)
  Support = -> [Pocket051]
  sketch-geometry (4):
    g0: LineSegment StartX=-1.55 StartY=1 StartZ=0 EndX=1.55 EndY=1 EndZ=0
    g1: LineSegment StartX=1.55 StartY=1 StartZ=0 EndX=1.55 EndY=-1 EndZ=0
    g2: LineSegment StartX=1.55 StartY=-1 StartZ=0 EndX=-1.55 EndY=-1 EndZ=0
    g3: LineSegment StartX=-1.55 StartY=-1 StartZ=0 EndX=-1.55 EndY=1 EndZ=0
  constraints (11):
    c: Coincident(g0,g1)
    c: Coincident(g1,g2)
    c: Coincident(g2,g3)
    c: Coincident(g3,g0)
    c: Horizontal(g0)
    c: Horizontal(g2)
    c: Vertical(g1)
    c: Vertical(g3)
    c: Symmetric(g0,g1,g-1)
    c: DistanceX(g0,g0) = 3.1
    c: DistanceY(g3,g3) = 2
FEATURE [PartDesign::Pocket] Pocket052  label="Pocket_EM-Grid_Grid-Slit"
  BaseFeature = -> Pocket051
  Length = 3.5
  Length2 = 100
  Profile = -> Sketch081
  Type = 0
FEATURE [Sketcher::SketchObject] Sketch082  label="Sketch_EM-Grid_Grid-Hole"
  MapMode = 5
  Placement = pos=(0,0,0) rot=(1,0,0;1.5708rad)
  Support = -> [XZ_Plane008]
  sketch-geometry (1):
    g0: Circle CenterX=0 CenterY=-10.8 CenterZ=0 NormalX=0 NormalY=0 NormalZ=1 AngleXU=0 Radius=1.45
  constraints (3):
    c: PointOnObject(g0,g-2)
    c: Radius(g0) = 1.45
    c: DistanceY(g0,g-1) = 10.8
FEATURE [PartDesign::Pocket] Pocket053  label="Pocket_EM-Grid_Grid-Hole"
  BaseFeature = -> Pocket052
  Length = 5
  Length2 = 5
  Profile = -> Sketch082
  Type = 4
FEATURE [Sketcher::SketchObject] Sketch083  label="Sketch_EM-Grid_Bottom_Hole"
  MapMode = 5
  Placement = pos=(0,0,-15) rot=(1,0,0;3.14159rad)
  Support = -> [Pocket053]
  sketch-geometry (1):
    g0: Circle CenterX=0 CenterY=0 CenterZ=0 NormalX=0 NormalY=0 NormalZ=1 AngleXU=0 Radius=1
  constraints (2):
    c: Coincident(g0,g-1)
    c: Radius(g0) = 1
FEATURE [PartDesign::Pocket] Pocket054  label="Pocket_EM-Grid_Bottom_Hole"
  BaseFeature = -> Pocket053
  Length = 5
  Length2 = 100
  Profile = -> Sketch083
  Type = 1
FEATURE [PartDesign::Body] Body008  label="Body_EM-Grid"
  Group = -> [Sketch079,Pad024,Sketch080,Pocket051,Sketch081,Pocket052,Sketch082,Pocket053,Sketch083,Pocket054]
  Origin = -> Origin008
  Placement = pos=(0,29.5,57.5) rot=(0,0,1;0rad)
  Tip = -> Pocket054
